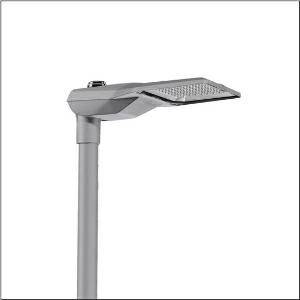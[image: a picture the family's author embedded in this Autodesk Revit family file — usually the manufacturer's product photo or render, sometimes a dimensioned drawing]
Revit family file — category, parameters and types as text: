
# Revit family: streetlight_sl_21_midi___st1_0a_5xe7d47n08lb_f0d9
name_source: partatom
category: Lighting Fixtures
units: mm (PartAtom-declared; Revit-internal decimal feet)

## family parameters
Cut with Voids When Loaded = No
Host = Face
Light Source = No
Part Type = Normal
Room Calculation Point = No
Round Connector Dimension = Use Diameter
Shared = No

## types (1)
- --- (1 x LED, 14950 lm, 98.3 W, 4000K)
    Apparent Load = 98 VA
    CIE Flux Codes = 37 72 97 100 100
    Color Rendering = 70
    Color Temperature = 4000K
    Default Elevation = 1800 mm
    Description = Streetlight SL 21 midi, mast luminaire, primary light control with lens, of PMMA, primary optical cover: cover, of toughened safety glass, transparent, light distribution: ST1.0a, light emission: direct distribution, primary light characteristic: asymmetric, installation type: side-entry, LED, 3G 2.5mm², High Power LED, rated luminous flux: 14.950lm, luminous efficacy: 152lm/W, light colour: 740, colour temperature: 4000K, control gear: NEMA (7pin), control: overheat protection, pre-setting: linear dimming characteristic, constant luminous flux control, time-dependent luminous flux control, flexible luminous flux parameterisation, mains connection: 220..240V, AC, 50/60Hz, connection cable pre-assembled, cable length: 10,5m, wiring characteristics: H05VV-F, start of lifetime: 98W, end of service life: 101W, reduction: 45W, luminaire housing, of diecast aluminium (EN AC-44300), powder-coated, SITECO metallic grey (DB 702S), corrosivity category C5 high according to DIN EN ISO 12944, multi-level sealing system, sealing non-destructively replaceable, inclination adjustable: 0°, 5°, 10°, 15°, length: 644mm, width: 335mm, height: 110mm, spigot size: 42mm (side-entry), mounting height: 4..8m, protection rating (complete): IP66, insulation class (complete): insulation class I (protective earthing), certification: CE, ENEC, ENEC+, VDE, impact resistance: IK10, permissible operating ambient temperature for outdoor applications: -40..+50°C, standard-compliant lighting for roads and squares, packaging unit: 1 piece

Light Distribution: ST1.0a
    Height = 111 mm
    Lamp = 1 x LED
    Lamp Light Flux = 14950 lm
    Lamp Power = 98.3 W
    Lamp count = 1
    Length = 644 mm
    Luminous efficacy = 152 lm/W
    Manufacturer = Siteco
    ModVariant = No
    Model = 5XE7D47N08LB
    Mounting Place = Pole
    Mounting Type = Pole top
    Number of Poles = 1
    OnlyDefault = Yes
    Power Factor = 1
    Product Name = Streetlight SL 21 midi | ST1.0a
    Product group = mast luminaire | pylon top
    ProductGroupID = 6100
    Protection Class = Protection class I
    Protection Degree = IP 66
    RLX_Detail_Level = 1
    RLX_Emergency_Light_Flux = 0 lm
    RLX_Emergency_Type = 0
    RLX_Emergency_Type_DB = No
    RlxData = <blob elided: 26713 chars, md5=b8e991f7>
    Socket = socket
    Standby Power = 0 W
    System Light Flux = 14950 lm
    System Power = 98 W
    Type Comments = factory setting: luminous flux: 100 % | dim-lin: 254 | 1020 mA
    Type Image = l_1294377.jpg
    URL = http://relux.com
    VarID = @adj_137059
    Voltage = 0 V
    Weight = 0.00 kg
    Width = 336 mm

## geometry (parser evidence)
native form markers: Blend x4, Sweep x11
no freeform markers — native parametric forms only
